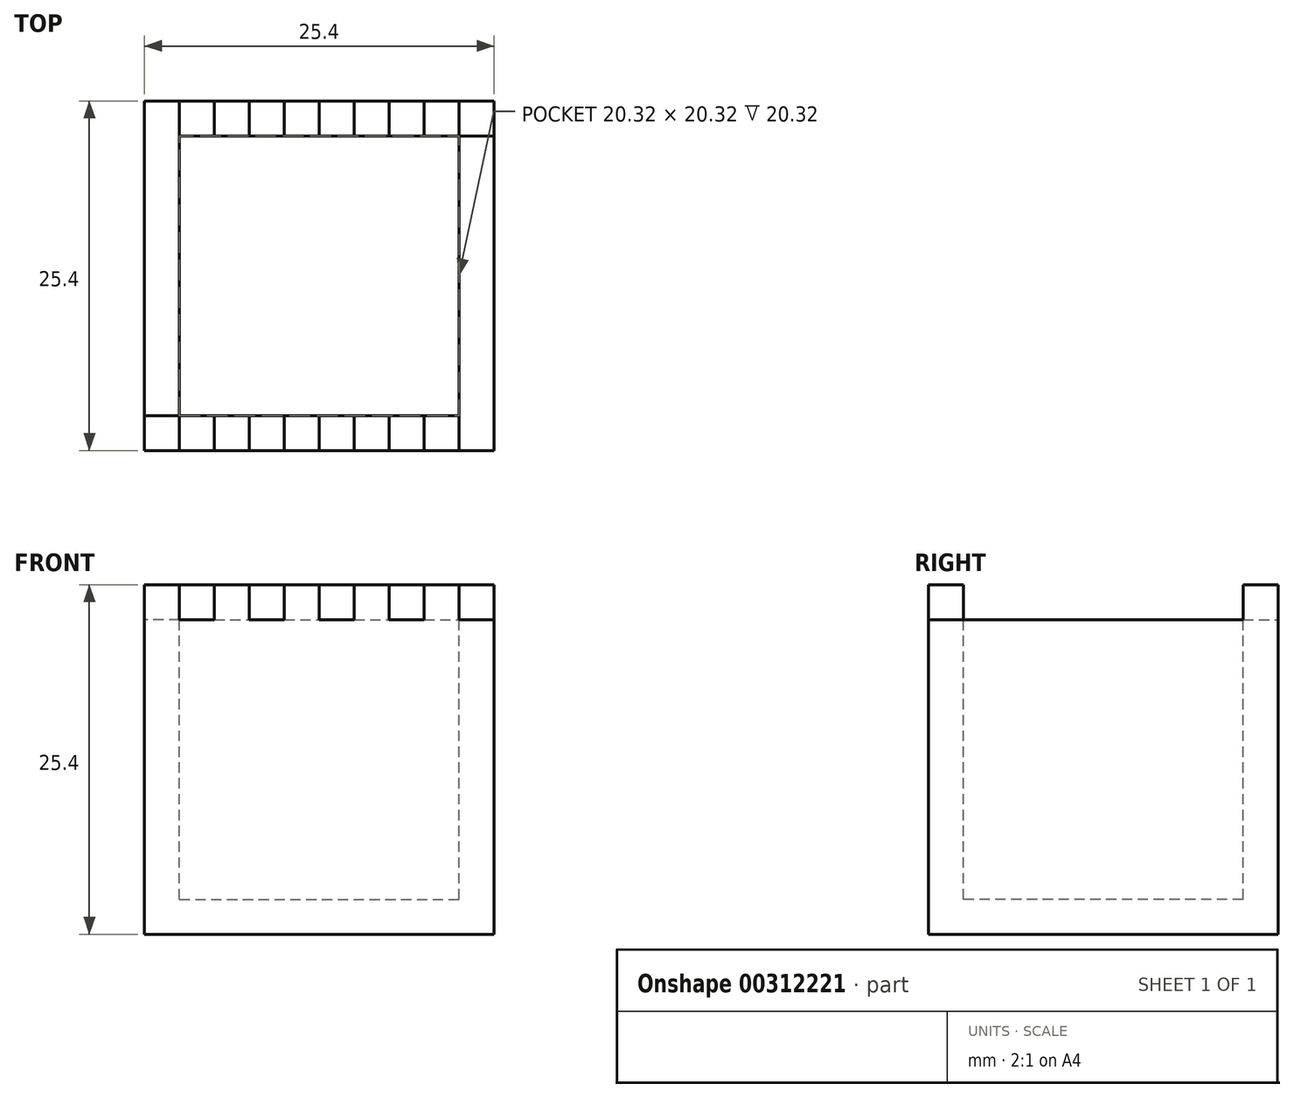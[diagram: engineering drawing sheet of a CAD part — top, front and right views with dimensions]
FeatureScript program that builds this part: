
annotation { "Feature Type Name" : "Feature", "Feature Type Description" : "" }
export const myFeature = defineFeature(function(context is Context, id is Id, definition is map)
    precondition{}
    {
        {
            var Q0;
            Q0=qCreatedBy(makeId("Top.planeOp"),FACE);
            var sketch = newSketch(context, id + "F0", { "sketchPlane" : qUnion([Q0])});
            skLineSegment(sketch, "E0.bottom", {"start": v(12.7, 12.7) * mm, "end": v(-12.7, 12.7) * mm});
            skLineSegment(sketch, "E0.top", {"start": v(12.7, -12.7) * mm, "end": v(-12.7, -12.7) * mm});
            skLineSegment(sketch, "E0.left", {"start": v(12.7, 12.7) * mm, "end": v(12.7, -12.7) * mm});
            skLineSegment(sketch, "E0.right", {"start": v(-12.7, 12.7) * mm, "end": v(-12.7, -12.7) * mm});
            skPoint(sketch, "E0.middle", {"position": v(0, 0) * mm});
            skSolve(sketch);
        }
        {
            var Q0;
            Q0=makeQuery(id+"F0.imprint","IMPRINT",FACE,{"disambiguationData":[TD([[makeQuery(id+"F0.imprint","IMPRINT",EDGE,{"derivedFrom":sQuery(id+"F0.wireOp",EDGE,"E0.bottom")}),1.0]])]});
            extrude(context, id + "F1", {"entities" : qUnion([Q0]), "depth" : 25.4 * mm});
        }
        {
            var Q0;
            Q0=makeQuery(id+"F1.opExtrude","CAP_FACE",FACE,{"disambiguationData":[OSD([sQuery(id+"F0.wireOp",EDGE,"E0.bottom"),sQuery(id+"F0.wireOp",EDGE,"E0.top"),sQuery(id+"F0.wireOp",EDGE,"E0.left"),sQuery(id+"F0.wireOp",EDGE,"E0.right")])],"isStart":false});
            var sketch = newSketch(context, id + "F2", { "sketchPlane" : qUnion([Q0])});
            skLineSegment(sketch, "E1", {"start": v(12.7, 12.7) * mm, "end": v(12.7, 10.16) * mm});
            skLineSegment(sketch, "E2", {"start": v(12.7, 12.7) * mm, "end": v(10.16, 12.7) * mm});
            skLineSegment(sketch, "E3", {"start": v(10.16, 12.7) * mm, "end": v(10.16, 10.16) * mm});
            skLineSegment(sketch, "E4", {"start": v(7.62, 10.16) * mm, "end": v(7.62, 12.7) * mm});
            skLineSegment(sketch, "E5", {"start": v(7.62, 12.7) * mm, "end": v(5.08, 12.7) * mm});
            skLineSegment(sketch, "E6", {"start": v(5.08, 12.7) * mm, "end": v(5.08, 10.16) * mm});
            skLineSegment(sketch, "E7", {"start": v(2.54, 10.16) * mm, "end": v(2.54, 12.7) * mm});
            skLineSegment(sketch, "E8", {"start": v(2.54, 12.7) * mm, "end": v(0, 12.7) * mm});
            skLineSegment(sketch, "E9", {"start": v(0, 12.7) * mm, "end": v(0, 10.16) * mm});
            skLineSegment(sketch, "E10", {"start": v(-2.54, 10.16) * mm, "end": v(-2.54, 12.7) * mm});
            skLineSegment(sketch, "E11", {"start": v(-2.54, 12.7) * mm, "end": v(-5.08, 12.7) * mm});
            skLineSegment(sketch, "E12", {"start": v(-5.08, 12.7) * mm, "end": v(-5.08, 10.16) * mm});
            skLineSegment(sketch, "E13", {"start": v(-7.62, 10.16) * mm, "end": v(-7.62, 12.7) * mm});
            skLineSegment(sketch, "E14", {"start": v(-7.62, 12.7) * mm, "end": v(-10.16, 12.7) * mm});
            skLineSegment(sketch, "E15", {"start": v(-10.16, 12.7) * mm, "end": v(-10.16, 10.16) * mm});
            skLineSegment(sketch, "E16", {"start": v(12.7, -12.7) * mm, "end": v(12.7, -10.16) * mm});
            skLineSegment(sketch, "E17", {"start": v(-12.7, -12.7) * mm, "end": v(-10.16, -12.7) * mm});
            skLineSegment(sketch, "E18", {"start": v(-10.16, -12.7) * mm, "end": v(-10.16, -10.16) * mm});
            skLineSegment(sketch, "E19", {"start": v(-7.62, -10.16) * mm, "end": v(-7.62, -12.7) * mm});
            skLineSegment(sketch, "E20", {"start": v(-7.62, -12.7) * mm, "end": v(-5.08, -12.7) * mm});
            skLineSegment(sketch, "E21", {"start": v(-5.08, -12.7) * mm, "end": v(-5.08, -10.16) * mm});
            skLineSegment(sketch, "E22", {"start": v(-2.54, -10.16) * mm, "end": v(-2.54, -12.7) * mm});
            skLineSegment(sketch, "E23", {"start": v(-2.54, -12.7) * mm, "end": v(0, -12.7) * mm});
            skLineSegment(sketch, "E24", {"start": v(0, -12.7) * mm, "end": v(0, -10.16) * mm});
            skLineSegment(sketch, "E25", {"start": v(2.54, -10.16) * mm, "end": v(2.54, -12.7) * mm});
            skLineSegment(sketch, "E26", {"start": v(2.54, -12.7) * mm, "end": v(5.08, -12.7) * mm});
            skLineSegment(sketch, "E27", {"start": v(5.08, -12.7) * mm, "end": v(5.08, -10.16) * mm});
            skLineSegment(sketch, "E28", {"start": v(7.62, -10.16) * mm, "end": v(7.62, -12.7) * mm});
            skLineSegment(sketch, "E29", {"start": v(7.62, -12.7) * mm, "end": v(10.16, -12.7) * mm});
            skLineSegment(sketch, "E30", {"start": v(10.16, -12.7) * mm, "end": v(10.16, -10.16) * mm});
            skLineSegment(sketch, "E31", {"start": v(-12.7, 12.7) * mm, "end": v(-12.7, 10.16) * mm});
            skLineSegment(sketch, "E32", {"start": v(-12.7, 12.7) * mm, "end": v(12.7, 12.7) * mm});
            skLineSegment(sketch, "E33", {"start": v(12.7, -12.7) * mm, "end": v(-12.7, -12.7) * mm});
            skLineSegment(sketch, "E34", {"start": v(-10.16, 10.16) * mm, "end": v(-7.62, 10.16) * mm});
            skLineSegment(sketch, "E35", {"start": v(10.16, -10.16) * mm, "end": v(7.62, -10.16) * mm});
            skLineSegment(sketch, "E36", {"start": v(-10.16, -10.16) * mm, "end": v(-12.7, -10.16) * mm});
            skLineSegment(sketch, "E37", {"start": v(-12.7, -10.16) * mm, "end": v(-12.7, -12.7) * mm});
            skLineSegment(sketch, "E38", {"start": v(10.16, 10.16) * mm, "end": v(12.7, 10.16) * mm});
            skLineSegment(sketch, "E39.trimOffspring", {"start": v(5.08, -10.16) * mm, "end": v(2.54, -10.16) * mm});
            skLineSegment(sketch, "E40.trimOffspring", {"start": v(5.08, 10.16) * mm, "end": v(7.62, 10.16) * mm});
            skLineSegment(sketch, "E41.trimOffspring", {"start": v(0, -10.16) * mm, "end": v(-2.54, -10.16) * mm});
            skLineSegment(sketch, "E42.trimOffspring", {"start": v(0, 10.16) * mm, "end": v(2.54, 10.16) * mm});
            skLineSegment(sketch, "E43.trimOffspring", {"start": v(-5.08, -10.16) * mm, "end": v(-7.62, -10.16) * mm});
            skLineSegment(sketch, "E44.trimOffspring", {"start": v(-5.08, 10.16) * mm, "end": v(-2.54, 10.16) * mm});
            skSolve(sketch);
        }
        {
            var Q0;
            {var subQ1=sQuery(id+"F2.wireOp",EDGE,"E3");Q0=makeQuery(id+"F2.imprint","IMPRINT",FACE,{"disambiguationData":[TD([[makeQuery(id+"F2.imprint","IMPRINT",EDGE,{"derivedFrom":subQ1}),-1.0]])]});}
            extrude(context, id + "F3", {"entities" : qUnion([Q0]), "operationType" : NewBodyOperationType.REMOVE, "oppositeDirection" : true, "depth" : 2.54 * mm});
        }
        {
            var Q0;
            Q0=makeQuery(id+"F3.boolean.opBoolean","COPY",FACE,{"derivedFrom":makeQuery(id+"F3.opExtrude","CAP_FACE",FACE,{"disambiguationData":[OSD([sQuery(id+"F0.wireOp",EDGE,"E0.left"),sQuery(id+"F0.wireOp",EDGE,"E0.right"),sQuery(id+"F2.wireOp",EDGE,"E3"),sQuery(id+"F2.wireOp",EDGE,"E4"),sQuery(id+"F2.wireOp",EDGE,"E6"),sQuery(id+"F2.wireOp",EDGE,"E7"),sQuery(id+"F2.wireOp",EDGE,"E9"),sQuery(id+"F2.wireOp",EDGE,"E10"),sQuery(id+"F2.wireOp",EDGE,"E12"),sQuery(id+"F2.wireOp",EDGE,"E13"),sQuery(id+"F2.wireOp",EDGE,"E15"),sQuery(id+"F2.wireOp",EDGE,"E16"),sQuery(id+"F2.wireOp",EDGE,"E18"),sQuery(id+"F2.wireOp",EDGE,"E19"),sQuery(id+"F2.wireOp",EDGE,"E21"),sQuery(id+"F2.wireOp",EDGE,"E22"),sQuery(id+"F2.wireOp",EDGE,"E24"),sQuery(id+"F2.wireOp",EDGE,"E25"),sQuery(id+"F2.wireOp",EDGE,"E27"),sQuery(id+"F2.wireOp",EDGE,"E28"),sQuery(id+"F2.wireOp",EDGE,"E30"),sQuery(id+"F2.wireOp",EDGE,"E31"),sQuery(id+"F2.wireOp",EDGE,"E32"),sQuery(id+"F2.wireOp",EDGE,"E33"),sQuery(id+"F2.wireOp",EDGE,"E34"),sQuery(id+"F2.wireOp",EDGE,"E35"),sQuery(id+"F2.wireOp",EDGE,"E36"),sQuery(id+"F2.wireOp",EDGE,"E38"),sQuery(id+"F2.wireOp",EDGE,"E39.trimOffspring"),sQuery(id+"F2.wireOp",EDGE,"E40.trimOffspring"),sQuery(id+"F2.wireOp",EDGE,"E41.trimOffspring"),sQuery(id+"F2.wireOp",EDGE,"E42.trimOffspring"),sQuery(id+"F2.wireOp",EDGE,"E43.trimOffspring"),sQuery(id+"F2.wireOp",EDGE,"E44.trimOffspring")])],"isStart":false})});
            var sketch = newSketch(context, id + "F4", { "sketchPlane" : qUnion([Q0])});
            skLineSegment(sketch, "E45.bottom", {"start": v(10.16, 10.16) * mm, "end": v(-10.16, 10.16) * mm});
            skLineSegment(sketch, "E45.top", {"start": v(10.16, -10.16) * mm, "end": v(-10.16, -10.16) * mm});
            skLineSegment(sketch, "E45.left", {"start": v(10.16, 10.16) * mm, "end": v(10.16, -10.16) * mm});
            skLineSegment(sketch, "E45.right", {"start": v(-10.16, 10.16) * mm, "end": v(-10.16, -10.16) * mm});
            skPoint(sketch, "E45.middle", {"position": v(0, 0) * mm});
            skSolve(sketch);
        }
        {
            var Q0;
            {var subQ3=sQuery(id+"F4.wireOp",EDGE,"E45.left");Q0=makeQuery(id+"F4.imprint","IMPRINT",FACE,{"disambiguationData":[TD([[makeQuery(id+"F4.imprint","IMPRINT",EDGE,{"derivedFrom":subQ3}),-1.0]])]});}
            extrude(context, id + "F5", {"entities" : qUnion([Q0]), "operationType" : NewBodyOperationType.REMOVE, "oppositeDirection" : true, "depth" : 20.32 * mm});
        }
    });
